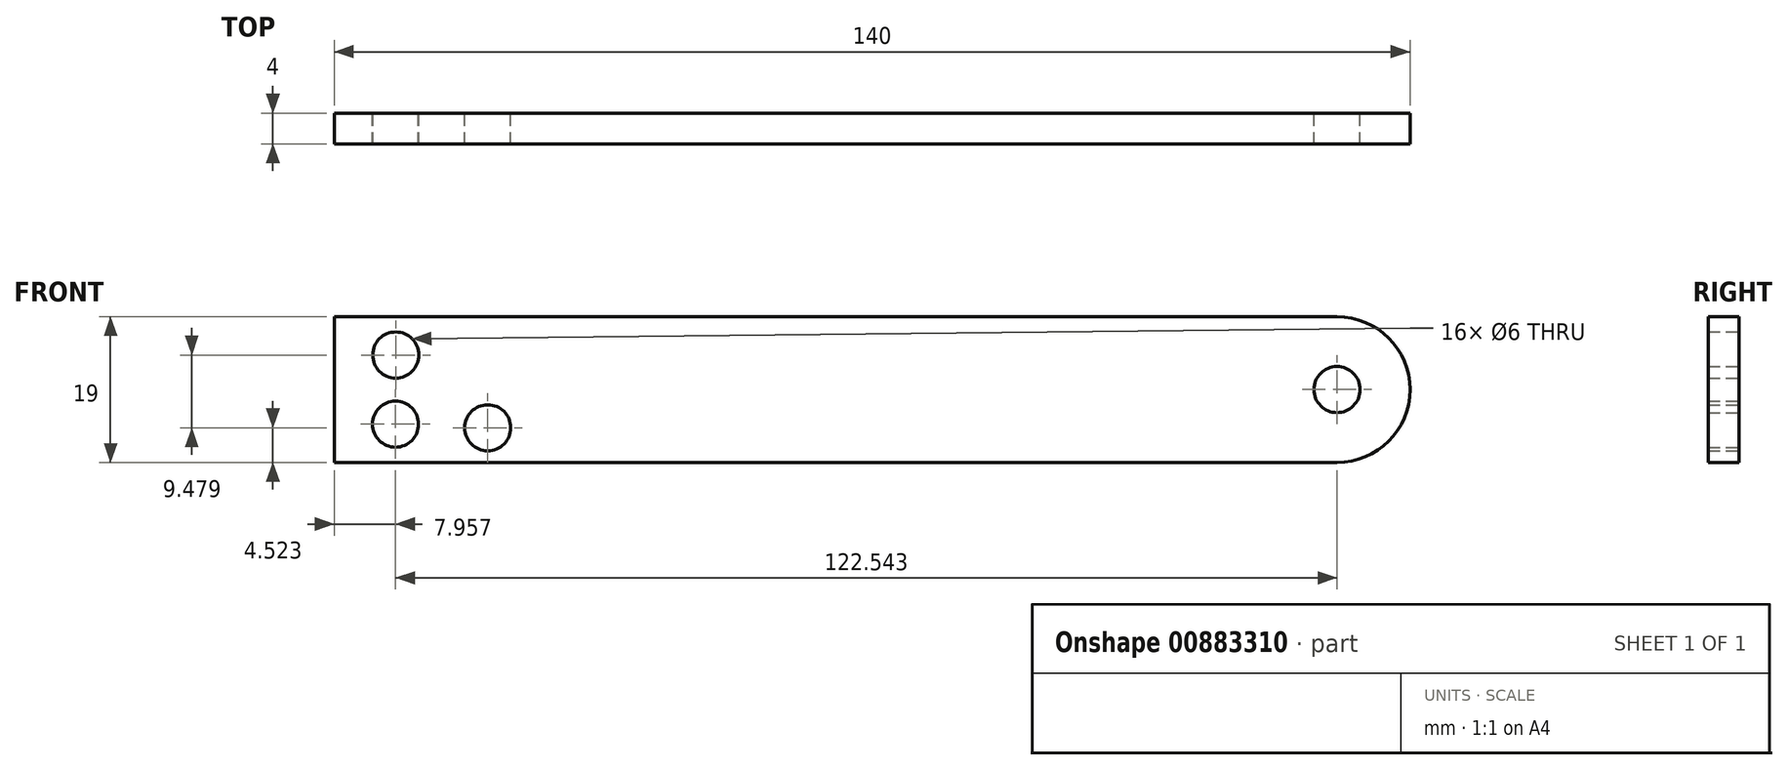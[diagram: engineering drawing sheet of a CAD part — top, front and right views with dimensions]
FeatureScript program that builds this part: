
annotation { "Feature Type Name" : "Feature", "Feature Type Description" : "" }
export const myFeature = defineFeature(function(context is Context, id is Id, definition is map)
    precondition{}
    {
        {
            var Q0;
            Q0=qCreatedBy(makeId("Front.planeOp"),FACE);
            var sketch = newSketch(context, id + "F0", { "sketchPlane" : qUnion([Q0])});
            skLineSegment(sketch, "E0.bottom", {"start": v(-11.93, -8.28) * mm, "end": v(128.07, -8.28) * mm});
            skLineSegment(sketch, "E0.top", {"start": v(-11.93, 10.72) * mm, "end": v(128.07, 10.72) * mm});
            skLineSegment(sketch, "E0.left", {"start": v(-11.93, -8.28) * mm, "end": v(-11.93, 10.72) * mm});
            skLineSegment(sketch, "E0.right", {"start": v(128.07, -8.28) * mm, "end": v(128.07, 10.72) * mm});
            skArc(sketch, "E1", {"start": v(118.57, -8.28) * mm, "mid": v(128.07, 1.22) * mm, "end": v(118.57, 10.72) * mm});
            skCircle(sketch, "E2", {"center": v(118.57, 1.22) * mm, "radius": 3 * mm});
            skCircle(sketch, "E3", {"center": v(-3.93, 5.72) * mm, "radius": 3 * mm});
            skCircle(sketch, "E4", {"center": v(-3.97, -3.28) * mm, "radius": 3 * mm});
            skCircle(sketch, "E5", {"center": v(8.03, -3.76) * mm, "radius": 3 * mm});
            skSolve(sketch);
        }
        {
            var Q0;
            {var subQ0=sQuery(id+"F0.wireOp",EDGE,"E0.left");Q0=makeQuery(id+"F0.imprint","IMPRINT",FACE,{"disambiguationData":[TD([[makeQuery(id+"F0.imprint","IMPRINT",EDGE,{"derivedFrom":subQ0}),-1.0]])]});}
            extrude(context, id + "F1", {"entities" : qUnion([Q0]), "depth" : 4 * mm, "offsetDistance" : 25 * mm});
        }
    });
